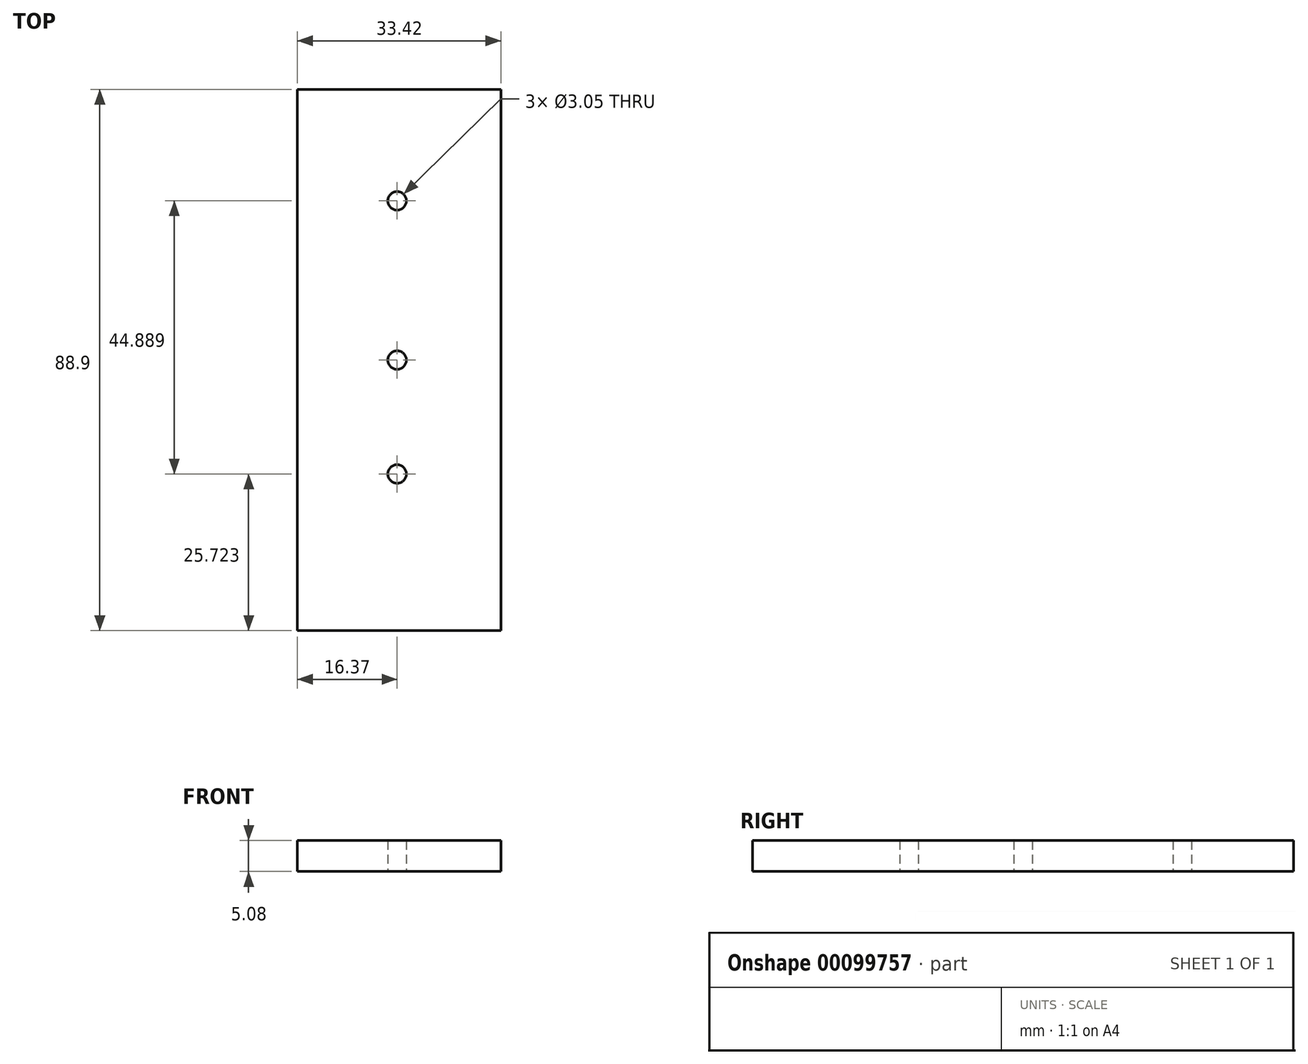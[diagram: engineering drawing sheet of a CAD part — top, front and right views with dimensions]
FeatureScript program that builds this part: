
annotation { "Feature Type Name" : "Feature", "Feature Type Description" : "" }
export const myFeature = defineFeature(function(context is Context, id is Id, definition is map)
    precondition{}
    {
        {
            var Q0;
            Q0=qCreatedBy(makeId("Top.planeOp"),FACE);
            var sketch = newSketch(context, id + "F0", { "sketchPlane" : qUnion([Q0])});
            skLineSegment(sketch, "E0.bottom", {"start": v(-16.37, 44.45) * mm, "end": v(17.05, 44.45) * mm});
            skLineSegment(sketch, "E0.top", {"start": v(-16.37, -44.45) * mm, "end": v(17.05, -44.45) * mm});
            skLineSegment(sketch, "E0.left", {"start": v(-16.37, 44.45) * mm, "end": v(-16.37, -44.45) * mm});
            skLineSegment(sketch, "E0.right", {"start": v(17.05, 44.45) * mm, "end": v(17.05, -44.45) * mm});
            skCircle(sketch, "E1", {"center": v(0, 26.16) * mm, "radius": 1.52 * mm});
            skCircle(sketch, "E2", {"center": v(0, 0) * mm, "radius": 1.52 * mm});
            skCircle(sketch, "E3", {"center": v(0, -18.73) * mm, "radius": 1.52 * mm});
            skSolve(sketch);
        }
        {
            var Q0;
            Q0=makeQuery(id+"F0.imprint","IMPRINT",FACE,{"disambiguationData":[TD([[makeQuery(id+"F0.imprint","IMPRINT",EDGE,{"derivedFrom":sQuery(id+"F0.wireOp",EDGE,"E0.bottom")}),-1.0]])]});
            extrude(context, id + "F1", {"entities" : qUnion([Q0]), "depth" : 5.08 * mm});
        }
    });
